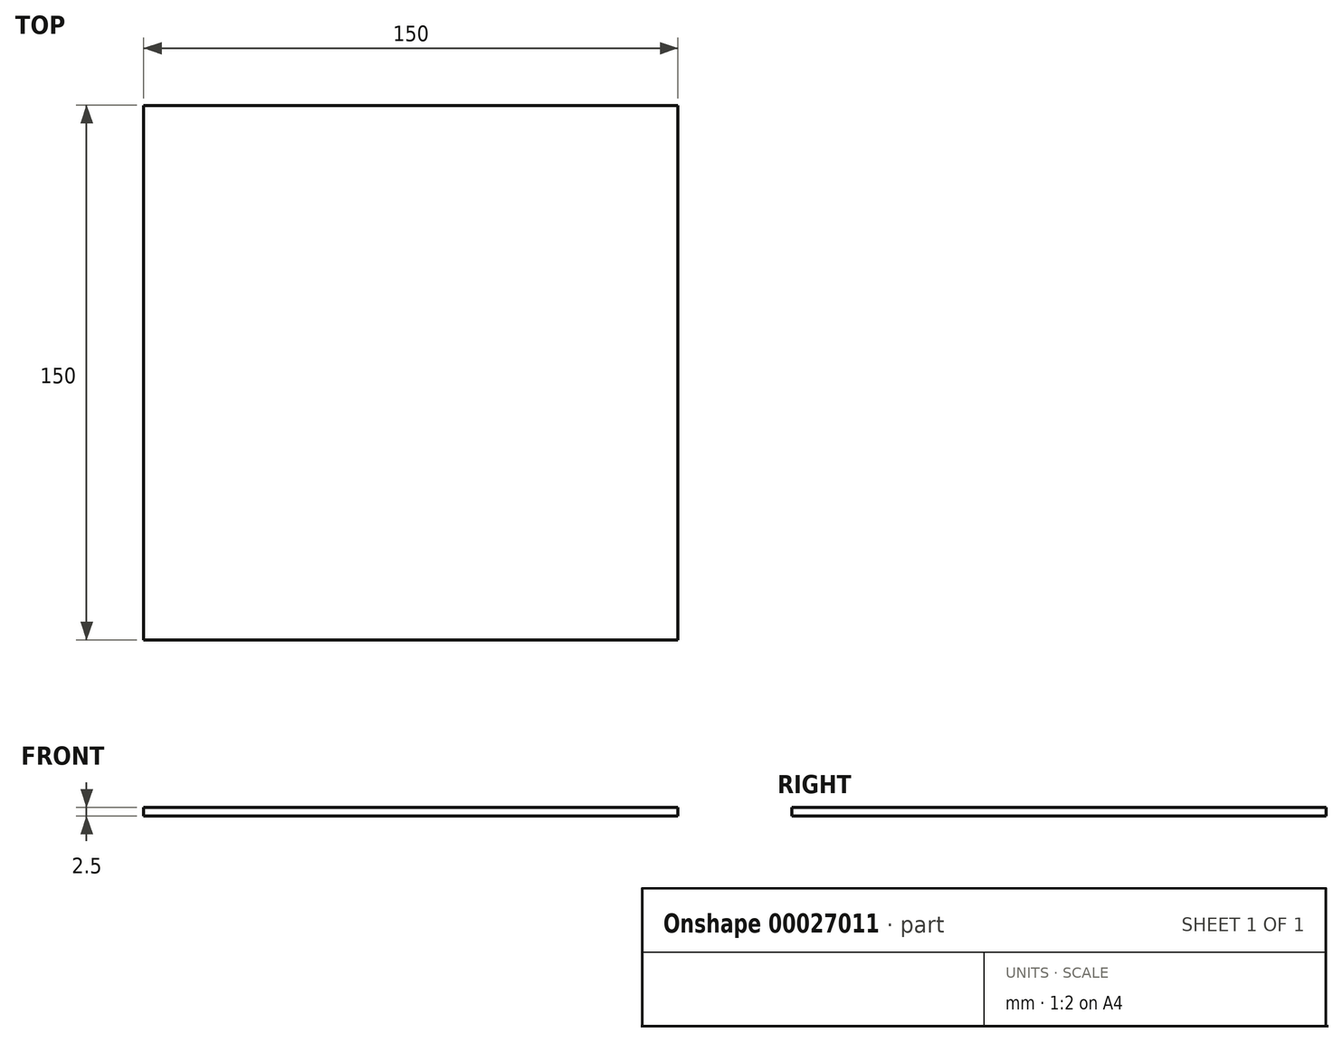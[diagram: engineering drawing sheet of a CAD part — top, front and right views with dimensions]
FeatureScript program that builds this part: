
annotation { "Feature Type Name" : "Feature", "Feature Type Description" : "" }
export const myFeature = defineFeature(function(context is Context, id is Id, definition is map)
    precondition{}
    {
        {
            var Q0;
            Q0=qCreatedBy(makeId("Top.planeOp"),FACE);
            var sketch = newSketch(context, id + "F0", { "sketchPlane" : qUnion([Q0])});
            skLineSegment(sketch, "E0.bottom", {"start": v(-37.89, 104.1) * mm, "end": v(112.11, 104.1) * mm});
            skLineSegment(sketch, "E0.top", {"start": v(-37.89, -45.9) * mm, "end": v(112.11, -45.9) * mm});
            skLineSegment(sketch, "E0.left", {"start": v(-37.89, 104.1) * mm, "end": v(-37.89, -45.9) * mm});
            skLineSegment(sketch, "E0.right", {"start": v(112.11, 104.1) * mm, "end": v(112.11, -45.9) * mm});
            skSolve(sketch);
        }
        {
            var Q0;
            Q0=makeQuery(id+"F0.imprint","IMPRINT",FACE,{"disambiguationData":[TD([[makeQuery(id+"F0.imprint","IMPRINT",EDGE,{"derivedFrom":sQuery(id+"F0.wireOp",EDGE,"E0.bottom")}),-1.0]])]});
            extrude(context, id + "F1", {"entities" : qUnion([Q0]), "endBound" : BoundingType.SYMMETRIC, "depth" : 2.5 * mm});
        }
    });
